# Revit family: LEGRAND_ECLAIRAGE_DE_SECURITE_SATI_CONNECTE
name_source: partatom
category: Luminaires
units: mm (PartAtom-declared; Revit-internal decimal feet)

## family parameters
Cote de connecteur circulaire = Utiliser le diamètre
Couper avec des vides une fois chargée = Non
Hôte = Face
Partagée = Non
Point de calcul de pièce = Non
Source d'éclairage = Non
Type d'élément = Normal

## types (8) — shared parameters
Accessoire non disponible = Pas d'accessoire ou Non disponible
Alimentation = décentralisé (batterie individuelle)
Classe de protection = II
Condition Générale d'Utilisation = https://export.legrand.com
Couleur du boitier = blanc
Elévation par défaut = 1219 mm
Etat des accus = NiMh
Fabricant = LEGRAND
Forme alternative = IP_43-66 : IP_43
Fréquence (Hz) = 50-60
Installation de surveillance = auto-test automatique
Largeur = 125 mm  [stored 0.410105 ft]
Longueur = 225 mm  [stored 0.738189 ft]
Matériau du boitier = LEGRAND - Plastique
Objet connecté = Oui
Porte_picto = Porte picto Triangulaire Ref 062676
Source lumineuse = LED non interchangeable
Température utilisation (Min-Max °C) = -5-35
Tension nominale (Min-Max V) = 207-253
Type de borne = borne automatique
Type de commutation = mode veille
Type de montage = montage en saillie-encastrement
Type de tension = CA
URL = http://www.legrandoc.com
zero-valued in all types: Diamètre externe

## per-type parameters (varying)
| type | Accessoire 1 | Accessoire 2 | Accessoire 3 | Accessoire 4 | Adapté au style de marquage | Autonomie (H) | Batterie rechange | Classe de protection (IP) | Consommation veille (mA) | Description | Entre axe fixation horizontale (Min-Max) (mm) | Entre axe fixation verticale (Min-Max) (mm) | Flux lumineux en mode d'urgence (lm) | Form | Hauteur-Profondeur | IP 66 | Largeur de montage | Longeur d'encastrement | Modèle | Picto | Profondeur d'encastrement | Puissance de la lampe (W) | Resistance aux chocs IK |
| Amb_IP43 | Encastrement sans plaque Ref 062694 | Suspension BAES et LSC Ref 062677 | Pas d'accessoire ou Non disponible | Pas d'accessoire ou Non disponible | autre | 1 | 061081 | IP43 | 5.5 | BAES AMBIANCE A LEDS  400LM  IP43 IK07 SATI CONNECTE | 60-95 | 0-65.5 | 400 | IP_43-66 : IP_43 | 45 mm  [stored 0.147638 ft] | Non | 160 mm  [stored 0.524934 ft] | 275 mm | 062565 | Pas de picto | 55 mm  [stored 0.180446 ft] | 4 | IK07 |
| BAEH_IP43 | Encastrement sans plaque Ref 062694 | Porte picto Vertical Ref 062675 | Suspension avec plaque BAES et LSC Ref 062677+062675 | Suspension BAES et LSC Ref 062677 | autre | 5 | 061080 | IP43 | 3 | BAEH HABITATION A LEDS PLASTIQUE IP43 IK07 SATI CONNECTE | 60-95 | 0-65.5 | 8 | IP_43-66 : IP_43 | 45 mm  [stored 0.147638 ft] | Non | 160 mm  [stored 0.524934 ft] | 275 mm | 062550 | Pas de picto | 55 mm  [stored 0.180446 ft] | 0.5 | IK07 |
| BAES+BAEH_IP43 | Encastrement sans plaque Ref 062694 | Porte picto Vertical Ref 062675 | Suspension avec plaque BAES et LSC Ref 062677+062675 | Suspension BAES et LSC Ref 062677 | feuillet-plaque inséré(e) | 1 | 2 x 061080 | IP43 | 4 | BAES + BAEH EVACUATION A LEDS PLASTIQUE IP43 IK 07 SATI CONNECTE | 60-95 | 0-65.5 | 45 | IP_43-66 : IP_43 | 45 mm  [stored 0.147638 ft] | Non | 160 mm  [stored 0.524934 ft] | 275 mm | 062560 | Picto Evac | 55 mm  [stored 0.180446 ft] | 1 | IK07 |
| Evac_IP43 | Encastrement sans plaque Ref 062694 | Porte picto Vertical Ref 062675 | Suspension avec plaque BAES et LSC Ref 062677+062675 | Suspension BAES et LSC Ref 062677 | feuillet-plaque inséré(e) | 1 | 061080 | IP43 | 3 | BAES EVACUATION A LEDS  IP43 IK07 SATI CONNECTE | 60-95 | 0-65.5 | 45 | IP_43-66 : IP_43 | 45 mm  [stored 0.147638 ft] | Non | 160 mm  [stored 0.524934 ft] | 275 mm | 062525 | Picto Evac | 55 mm  [stored 0.180446 ft] | 0.5 | IK07 |
| Amb_IP66 | Pas d'accessoire ou Non disponible | Pas d'accessoire ou Non disponible | Pas d'accessoire ou Non disponible | Pas d'accessoire ou Non disponible | autre | 1 | 061081 | IP66 | 5.5 | BAES AMBIANCE LEDS PLASTIQUE IP66 IK10 SATI CONNECTE | 80-153 | 0-83 | 400 | IP_43-66 : IP_66 | 62 mm  [stored 0.203412 ft] | Oui | 0 mm  [stored 0 ft] | 0 mm  [stored 0 ft] | 062566 | Pas de picto | 0 mm  [stored 0 ft] | 4 | IK10 |
| BAEH_IP66 | Porte picto Triangulaire Ref 062676 | Pas d'accessoire ou Non disponible | Pas d'accessoire ou Non disponible | Pas d'accessoire ou Non disponible | autre | 5 | 061080 | IP66 | 3 | BAEH HABITATION A LEDS  PLASTIQUE IP66 IK10 SATI CONNECTE | 80-153 | 0-83 | 8 | IP_43-66 : IP_66 | 62 mm  [stored 0.203412 ft] | Oui | 0 mm  [stored 0 ft] | 0 mm  [stored 0 ft] | 062552 | Pas de picto | 0 mm  [stored 0 ft] | 0.5 | IK10 |
| BAES+BAEH_IP66 | Porte picto Triangulaire Ref 062676 | Pas d'accessoire ou Non disponible | Pas d'accessoire ou Non disponible | Pas d'accessoire ou Non disponible | feuillet-plaque inséré(e) | 1 | 2 x 061080 | IP66 | 4 | BAES+BAEH EVACUATION A LEDS PLASTIQUE IP66 IK10 SATI CONNECTE | 80-153 | 0-83 | 45 | IP_43-66 : IP_66 | 62 mm  [stored 0.203412 ft] | Oui | 0 mm  [stored 0 ft] | 0 mm  [stored 0 ft] | 062561 | Picto Evac | 0 mm  [stored 0 ft] | 1 | IK10 |
| Evac_IP66 | Porte picto Triangulaire Ref 062676 | Pas d'accessoire ou Non disponible | Pas d'accessoire ou Non disponible | Pas d'accessoire ou Non disponible | feuillet-plaque inséré(e) | 1 | 061080 | IP66 | 3 | BAES EVACUATION A LEDS PLASTIQUE IP66 IK10 SATI CONNECTE | 80-153 | 0-83 | 45 | IP_43-66 : IP_66 | 62 mm  [stored 0.203412 ft] | Oui | 0 mm  [stored 0 ft] | 0 mm  [stored 0 ft] | 062526 | Picto Evac | 0 mm  [stored 0 ft] | 0.5 | IK10 |

note: [stored X ft] marks values corroborated as IEEE doubles in the binary element streams (Revit-internal decimal feet)
